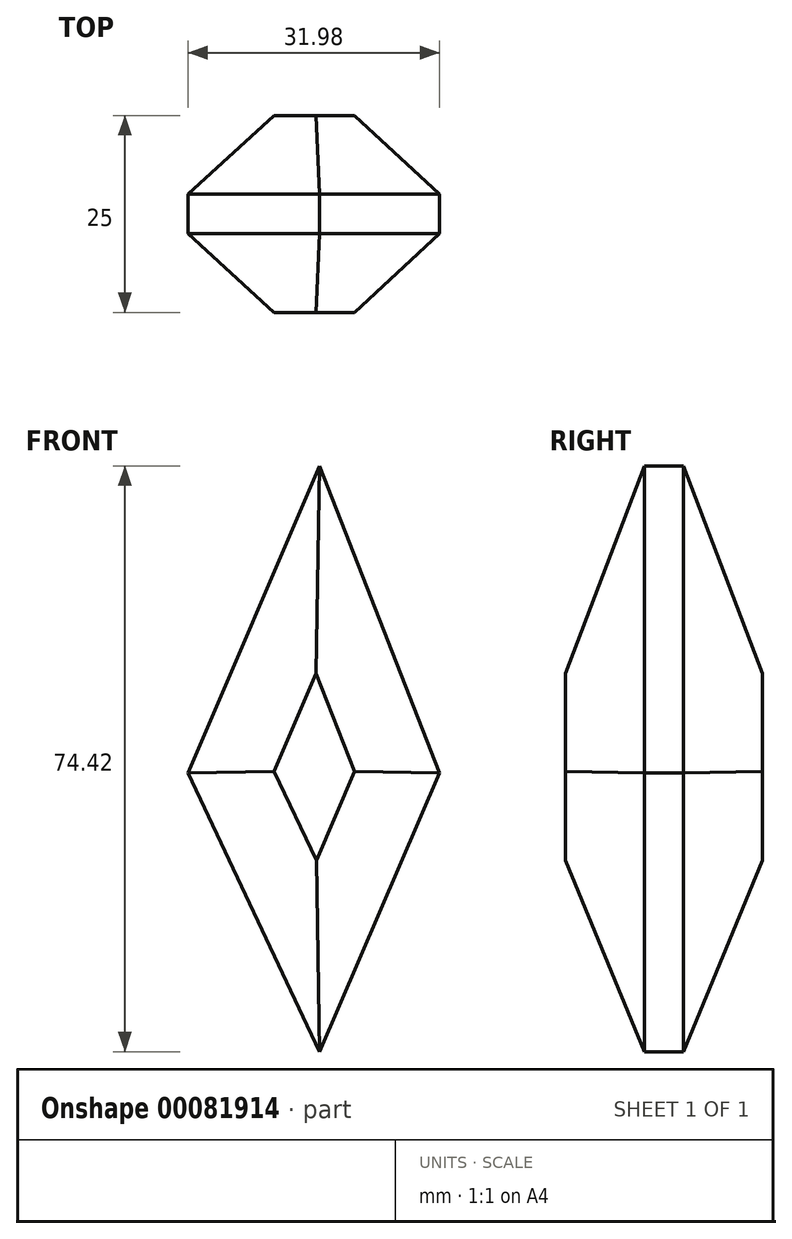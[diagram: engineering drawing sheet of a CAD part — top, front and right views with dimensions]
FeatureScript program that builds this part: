
annotation { "Feature Type Name" : "Feature", "Feature Type Description" : "" }
export const myFeature = defineFeature(function(context is Context, id is Id, definition is map)
    precondition{}
    {
        {
            var Q0;
            Q0=qCreatedBy(makeId("Front.planeOp"),FACE);
            var sketch = newSketch(context, id + "F0", { "sketchPlane" : qUnion([Q0])});
            skLineSegment(sketch, "E0", {"start": v(-16.74, 0) * mm, "end": v(0, 39) * mm});
            skLineSegment(sketch, "E1", {"start": v(0, 39) * mm, "end": v(15.24, 0) * mm});
            skLineSegment(sketch, "E2", {"start": v(15.24, 0) * mm, "end": v(0, -35.42) * mm});
            skLineSegment(sketch, "E3", {"start": v(0, -35.42) * mm, "end": v(-16.74, 0) * mm});
            skSolve(sketch);
        }
        {
            var Q0;
            Q0 = qSketchRegion(id + "F0", true);
            extrude(context, id + "F1", {"entities" : qUnion([Q0]), "depth" : 25 * mm});
        }
        {
            var Q0;
            Q0=makeQuery(id+"F1.opExtrude","CAP_EDGE",EDGE,{"disambiguationData":[OSD([sQuery(id+"F0.wireOp",EDGE,"E0")])],"isStart":false});
            var Q1;
            Q1=makeQuery(id+"F1.opExtrude","CAP_EDGE",EDGE,{"disambiguationData":[OSD([sQuery(id+"F0.wireOp",EDGE,"E0")])],"isStart":true});
            var Q2;
            Q2=makeQuery(id+"F1.opExtrude","CAP_EDGE",EDGE,{"disambiguationData":[OSD([sQuery(id+"F0.wireOp",EDGE,"E3")])],"isStart":false});
            var Q3;
            Q3=makeQuery(id+"F1.opExtrude","CAP_EDGE",EDGE,{"disambiguationData":[OSD([sQuery(id+"F0.wireOp",EDGE,"E3")])],"isStart":true});
            var Q4;
            Q4=makeQuery(id+"F1.opExtrude","CAP_EDGE",EDGE,{"disambiguationData":[OSD([sQuery(id+"F0.wireOp",EDGE,"E1")])],"isStart":true});
            var Q5;
            Q5=makeQuery(id+"F1.opExtrude","CAP_EDGE",EDGE,{"disambiguationData":[OSD([sQuery(id+"F0.wireOp",EDGE,"E1")])],"isStart":false});
            var Q6;
            Q6=makeQuery(id+"F1.opExtrude","CAP_EDGE",EDGE,{"disambiguationData":[OSD([sQuery(id+"F0.wireOp",EDGE,"E2")])],"isStart":false});
            var Q7;
            Q7=makeQuery(id+"F1.opExtrude","CAP_EDGE",EDGE,{"disambiguationData":[OSD([sQuery(id+"F0.wireOp",EDGE,"E2")])],"isStart":true});
            chamfer(context, id + "F2", {"entities" : qUnion([Q0, Q1, Q2, Q3, Q4, Q5, Q6, Q7]), "width" : 10 * mm, "tangentPropagation" : true});
        }
    });
